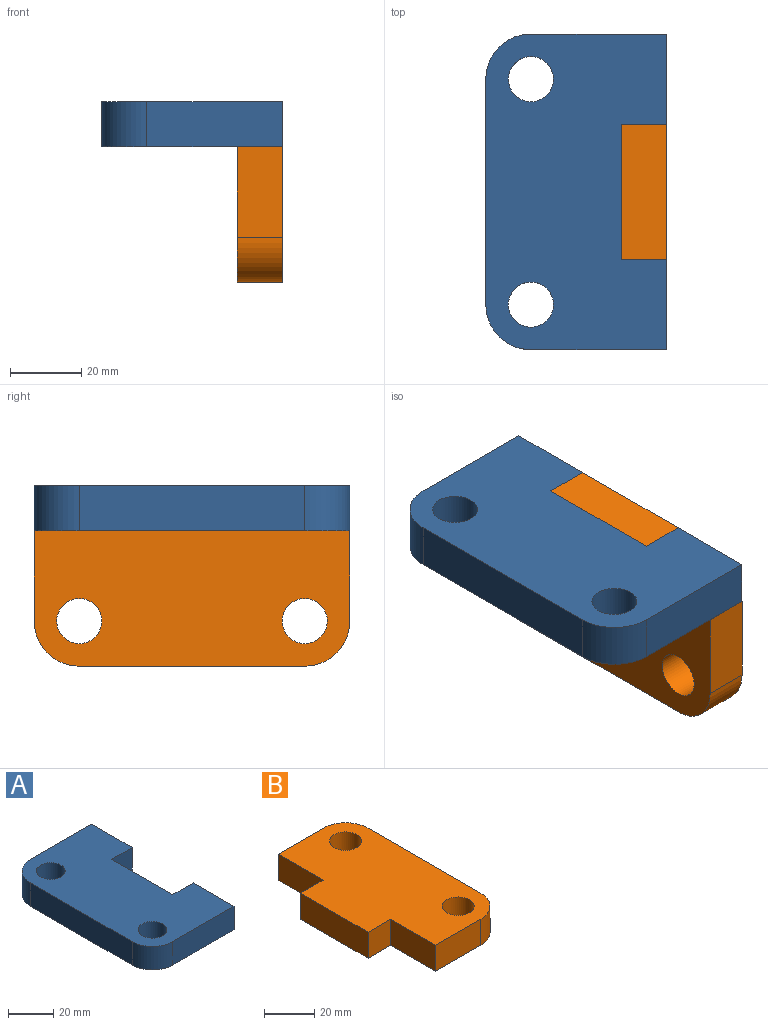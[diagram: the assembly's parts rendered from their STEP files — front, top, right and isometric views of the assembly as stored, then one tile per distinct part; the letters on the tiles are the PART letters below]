
ASSEMBLY  parts=2 mates=1
PART A: 14 faces, bbox 50.8x88.9x12.7 mm
  f0: plane 38.11x12.7mm, normal (1,0,0), area 484mm2, adj f4,f5,f10,f12
  f1: plane 63.5x12.7mm, normal (-1,0,0), area 806.5mm2, adj f4,f5,f6,f7
  f2: plane 38.1x12.7mm, normal (0,-1,0), area 483.9mm2, adj f4,f5,f6,f13
  f3: plane 38.1x12.7mm, normal (0,1,0), area 483.9mm2, adj f4,f5,f7,f11
  f4: plane 88.9x50.8mm, normal (0,0,1), area 3709.6mm2, adj f0,f1,f2,f3,f6,f7,f8,f9
  f5: plane 88.9x50.8mm, normal (0,0,-1), area 3709.6mm2, adj f0,f1,f2,f3,f6,f7,f8,f9
  f6: cylinder r=12.7mm len=12.7mm, axis (0,0,1), area 253.4mm2, adj f1,f2,f4,f5
  f7: cylinder r=12.7mm len=12.7mm, axis (0,0,-1), area 253.4mm2, adj f1,f3,f4,f5
  f8: cylinder r=6.35mm len=12.7mm, axis (0,0,1), area 506.7mm2, adj f4,f5
  f9: cylinder r=6.35mm len=12.7mm, axis (0,0,1), area 506.7mm2, adj f4,f5
  f10: plane 12.7x12.7mm, normal (0,-1,0), area 161.3mm2, adj f0,f4,f5,f11
  f11: plane 25.39x12.7mm, normal (1,0,0), area 322.5mm2, adj f3,f4,f5,f10
  f12: plane 12.7x12.7mm, normal (0,1,0), area 161.3mm2, adj f0,f4,f5,f13
  f13: plane 25.4x12.7mm, normal (1,0,0), area 322.6mm2, adj f2,f4,f5,f12
PART B: 14 faces, bbox 50.8x88.9x12.7 mm
  f0: plane 25.4x12.7mm, normal (-1,0,0), area 322.6mm2, adj f4,f5,f6,f11
  f1: plane 25.4x12.7mm, normal (-1,0,0), area 322.6mm2, adj f2,f5,f6,f12
  f2: plane 25.4x12.7mm, normal (0,-1,0), area 322.6mm2, adj f1,f5,f6,f7
  f3: plane 63.5x12.7mm, normal (1,0,0), area 806.5mm2, adj f5,f6,f7,f8
  f4: plane 25.4x12.7mm, normal (0,1,0), area 322.6mm2, adj f0,f5,f6,f8
  f5: plane 88.9x50.8mm, normal (0,0,1), area 3548.4mm2, adj f0,f1,f2,f3,f4,f7,f8,f9
  f6: plane 88.9x50.8mm, normal (0,0,-1), area 3548.4mm2, adj f0,f1,f2,f3,f4,f7,f8,f9
  f7: cylinder r=12.7mm len=12.7mm, axis (0,0,-1), area 253.4mm2, adj f2,f3,f5,f6
  f8: cylinder r=12.7mm len=12.7mm, axis (0,0,1), area 253.4mm2, adj f3,f4,f5,f6
  f9: cylinder r=6.35mm len=12.7mm, axis (0,0,1), area 506.7mm2, adj f5,f6
  f10: cylinder r=6.35mm len=12.7mm, axis (0,0,1), area 506.7mm2, adj f5,f6
  f11: plane 12.7x12.7mm, normal (0,1,0), area 161.3mm2, adj f0,f5,f6,f13
  f12: plane 12.7x12.7mm, normal (0,-1,0), area 161.3mm2, adj f1,f5,f6,f13
  f13: plane 38.1x12.7mm, normal (-1,0,0), area 483.9mm2, adj f5,f6,f11,f12
PLACE A t=(-31.49,-29.96,20.66)mm
PLACE B rot(axis=(0,1,0),90deg) t=(6.61,-29.96,20.66)mm
MATE pin_slot B.f12 <-> A.f12  axis (0,-1,0) through (19.31,-4.56,33.36)mm
